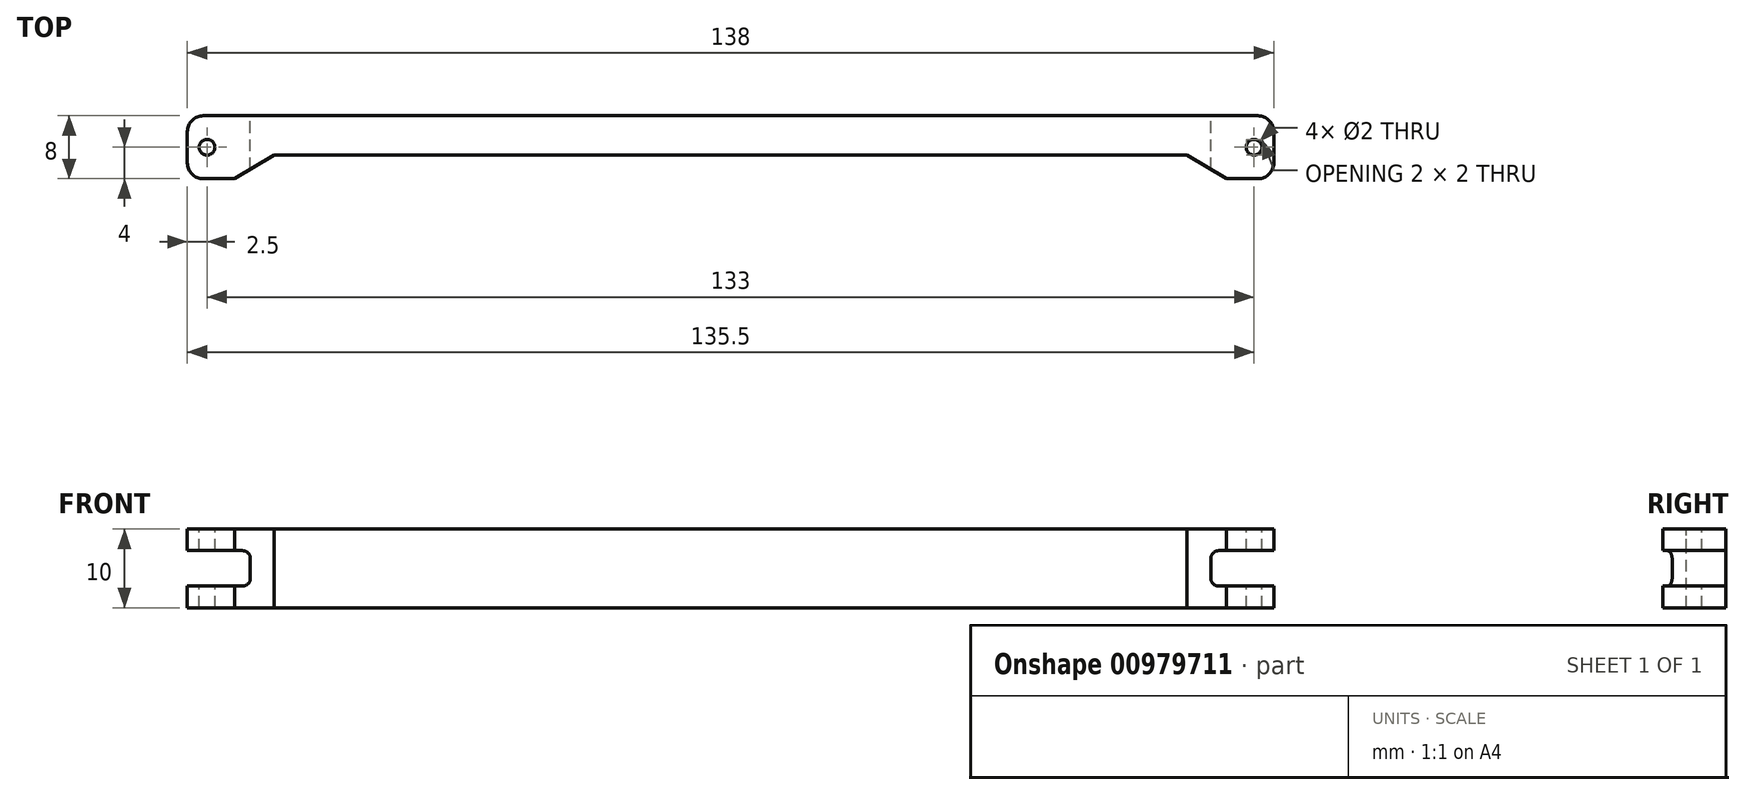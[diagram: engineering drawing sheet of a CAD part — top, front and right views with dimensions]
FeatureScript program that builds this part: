
annotation { "Feature Type Name" : "Feature", "Feature Type Description" : "" }
export const myFeature = defineFeature(function(context is Context, id is Id, definition is map)
    precondition{}
    {
        {
            var Q0;
            Q0=qCreatedBy(makeId("Front.planeOp"),FACE);
            var sketch = newSketch(context, id + "F0", { "sketchPlane" : qUnion([Q0])});
            skLineSegment(sketch, "E0.bottom", {"start": v(69, 5) * mm, "end": v(-69, 5) * mm});
            skLineSegment(sketch, "E0.top", {"start": v(69, -5) * mm, "end": v(-69, -5) * mm});
            skLineSegment(sketch, "E0.left", {"start": v(69, 5) * mm, "end": v(69, 2.25) * mm});
            skLineSegment(sketch, "E0.right", {"start": v(-69, 5) * mm, "end": v(-69, 2.25) * mm});
            skPoint(sketch, "E0.middle", {"position": v(0, 0) * mm});
            skLineSegment(sketch, "E1.bottom", {"start": v(-61, 2.25) * mm, "end": v(-69, 2.25) * mm});
            skLineSegment(sketch, "E1.top", {"start": v(-61, -2.25) * mm, "end": v(-69, -2.25) * mm});
            skLineSegment(sketch, "E1.left", {"start": v(-61, 2.25) * mm, "end": v(-61, -2.25) * mm});
            skPoint(sketch, "E1.middle", {"position": v(-69, 0) * mm});
            skLineSegment(sketch, "E2.trimOffspring", {"start": v(-69, -2.25) * mm, "end": v(-69, -5) * mm});
            skPoint(sketch, "E1.right.end.orphan", {"position": v(-77, -2.25) * mm});
            skPoint(sketch, "E1.right.start.orphan", {"position": v(-77, 2.25) * mm});
            skLineSegment(sketch, "E3.bottom", {"start": v(61, 2.25) * mm, "end": v(69, 2.25) * mm});
            skLineSegment(sketch, "E3.top", {"start": v(61, -2.25) * mm, "end": v(69, -2.25) * mm});
            skLineSegment(sketch, "E3.left", {"start": v(61, 2.25) * mm, "end": v(61, -2.25) * mm});
            skPoint(sketch, "E3.middle", {"position": v(69, 0) * mm});
            skPoint(sketch, "E4.orphan", {"position": v(77, 2.25) * mm});
            skPoint(sketch, "E5.orphan", {"position": v(77, -2.25) * mm});
            skLineSegment(sketch, "E6.trimOffspring", {"start": v(69, -2.25) * mm, "end": v(69, -5) * mm});
            skSolve(sketch);
        }
        {
            var Q0;
            Q0 = qSketchRegion(id + "F0", true);
            extrude(context, id + "F1", {"entities" : qUnion([Q0]), "endBound" : BoundingType.SYMMETRIC, "depth" : 8 * mm, "offsetDistance" : 25 * mm});
        }
        {
            var Q0;
            Q0=qCreatedBy(makeId("Top.planeOp"),FACE);
            var sketch = newSketch(context, id + "F2", { "sketchPlane" : qUnion([Q0])});
            skCircle(sketch, "E7", {"center": v(-66.5, 0) * mm, "radius": 1 * mm});
            skCircle(sketch, "E8", {"center": v(66.5, 0) * mm, "radius": 1 * mm});
            skSolve(sketch);
        }
        {
            var Q0;
            Q0 = qSketchRegion(id + "F2", true);
            extrude(context, id + "F3", {"entities" : qUnion([Q0]), "operationType" : NewBodyOperationType.REMOVE, "endBound" : BoundingType.THROUGH_ALL, "oppositeDirection" : true, "depth" : 25 * mm, "offsetDistance" : 25 * mm, "hasSecondDirection" : true, "secondDirectionBound" : SecondDirectionBoundingType.THROUGH_ALL, "secondDirectionOppositeDirection" : false, "secondDirectionDepth" : 25 * mm});
        }
        {
            var Q0;
            Q0=qCreatedBy(makeId("Top.planeOp"),FACE);
            var sketch = newSketch(context, id + "F4", { "sketchPlane" : qUnion([Q0])});
            skLineSegment(sketch, "E9.bottom", {"start": v(63, -11) * mm, "end": v(-63, -11) * mm});
            skLineSegment(sketch, "E9.top", {"start": v(63, -1) * mm, "end": v(-63, -1) * mm});
            skLineSegment(sketch, "E9.left", {"start": v(63, -11) * mm, "end": v(63, -1) * mm});
            skLineSegment(sketch, "E9.right", {"start": v(-63, -11) * mm, "end": v(-63, -1) * mm});
            skPoint(sketch, "E9.middle", {"position": v(0, -6) * mm});
            skSolve(sketch);
        }
        {
            var Q0;
            Q0 = qSketchRegion(id + "F4", true);
            extrude(context, id + "F5", {"entities" : qUnion([Q0]), "operationType" : NewBodyOperationType.REMOVE, "endBound" : BoundingType.SYMMETRIC, "depth" : 20 * mm, "offsetDistance" : 25 * mm});
        }
        {
            var Q0;
            {var subQ0=sQuery(id+"F4.wireOp",EDGE,"E9.top");var subQ1=sQuery(id+"F4.wireOp",EDGE,"E9.right");Q0=makeQuery(id+"F5.boolean.opBoolean","COPY",EDGE,{"disambiguationData":[TD([makeQuery(id+"F1.opExtrude","SWEPT_FACE",FACE,{"disambiguationData":[OSD([sQuery(id+"F0.wireOp",EDGE,"E0.bottom")])]})])],"derivedFrom":makeQuery(id+"F5.opExtrude","SWEPT_EDGE",EDGE,{"disambiguationData":[OSD([subQ0,subQ1])]})});}
            var Q1;
            {var subQ0=sQuery(id+"F4.wireOp",EDGE,"E9.top");var subQ1=sQuery(id+"F4.wireOp",EDGE,"E9.left");Q1=makeQuery(id+"F5.boolean.opBoolean","COPY",EDGE,{"disambiguationData":[TD([makeQuery(id+"F1.opExtrude","SWEPT_FACE",FACE,{"disambiguationData":[OSD([sQuery(id+"F0.wireOp",EDGE,"E0.bottom")])]})])],"derivedFrom":makeQuery(id+"F5.opExtrude","SWEPT_EDGE",EDGE,{"disambiguationData":[OSD([subQ0,subQ1])]})});}
            chamfer(context, id + "F6", {"entities" : qUnion([Q0, Q1]), "chamferType" : ChamferType.TWO_OFFSETS, "width1" : 5 * mm, "oppositeDirection" : false, "width2" : 3 * mm, "tangentPropagation" : true});
        }
        {
            var Q0;
            Q0=makeQuery(id+"F1.opExtrude","CAP_EDGE",EDGE,{"disambiguationData":[OSD([sQuery(id+"F0.wireOp",EDGE,"E0.right")])],"isStart":true});
            var Q1;
            Q1=makeQuery(id+"F1.opExtrude","CAP_EDGE",EDGE,{"disambiguationData":[OSD([sQuery(id+"F0.wireOp",EDGE,"E2.trimOffspring")])],"isStart":true});
            var Q2;
            Q2=makeQuery(id+"F1.opExtrude","CAP_EDGE",EDGE,{"disambiguationData":[OSD([sQuery(id+"F0.wireOp",EDGE,"E0.right")])],"isStart":false});
            var Q3;
            Q3=makeQuery(id+"F1.opExtrude","CAP_EDGE",EDGE,{"disambiguationData":[OSD([sQuery(id+"F0.wireOp",EDGE,"E2.trimOffspring")])],"isStart":false});
            var Q4;
            Q4=makeQuery(id+"F1.opExtrude","CAP_EDGE",EDGE,{"disambiguationData":[OSD([sQuery(id+"F0.wireOp",EDGE,"E0.left")])],"isStart":false});
            var Q5;
            Q5=makeQuery(id+"F1.opExtrude","CAP_EDGE",EDGE,{"disambiguationData":[OSD([sQuery(id+"F0.wireOp",EDGE,"E6.trimOffspring")])],"isStart":false});
            var Q6;
            Q6=makeQuery(id+"F1.opExtrude","CAP_EDGE",EDGE,{"disambiguationData":[OSD([sQuery(id+"F0.wireOp",EDGE,"E6.trimOffspring")])],"isStart":true});
            var Q7;
            Q7=makeQuery(id+"F1.opExtrude","CAP_EDGE",EDGE,{"disambiguationData":[OSD([sQuery(id+"F0.wireOp",EDGE,"E0.left")])],"isStart":true});
            fillet(context, id + "F7", {"entities" : qUnion([Q0, Q1, Q2, Q3, Q4, Q5, Q6, Q7]), "radius" : 2 * mm, "tangentPropagation" : true, "allowEdgeOverflow" : false});
        }
        {
            var Q0;
            Q0=makeQuery(id+"F1.opExtrude","SWEPT_EDGE",EDGE,{"disambiguationData":[OSD([sQuery(id+"F0.wireOp",EDGE,"E3.top"),sQuery(id+"F0.wireOp",EDGE,"E3.left")])]});
            var Q1;
            Q1=makeQuery(id+"F1.opExtrude","SWEPT_EDGE",EDGE,{"disambiguationData":[OSD([sQuery(id+"F0.wireOp",EDGE,"E3.bottom"),sQuery(id+"F0.wireOp",EDGE,"E3.left")])]});
            var Q2;
            Q2=makeQuery(id+"F1.opExtrude","SWEPT_EDGE",EDGE,{"disambiguationData":[OSD([sQuery(id+"F0.wireOp",EDGE,"E1.bottom"),sQuery(id+"F0.wireOp",EDGE,"E1.left")])]});
            var Q3;
            Q3=makeQuery(id+"F1.opExtrude","SWEPT_EDGE",EDGE,{"disambiguationData":[OSD([sQuery(id+"F0.wireOp",EDGE,"E1.top"),sQuery(id+"F0.wireOp",EDGE,"E1.left")])]});
            fillet(context, id + "F8", {"entities" : qUnion([Q0, Q1, Q2, Q3]), "radius" : 1 * mm, "tangentPropagation" : true, "allowEdgeOverflow" : false});
        }
    });
